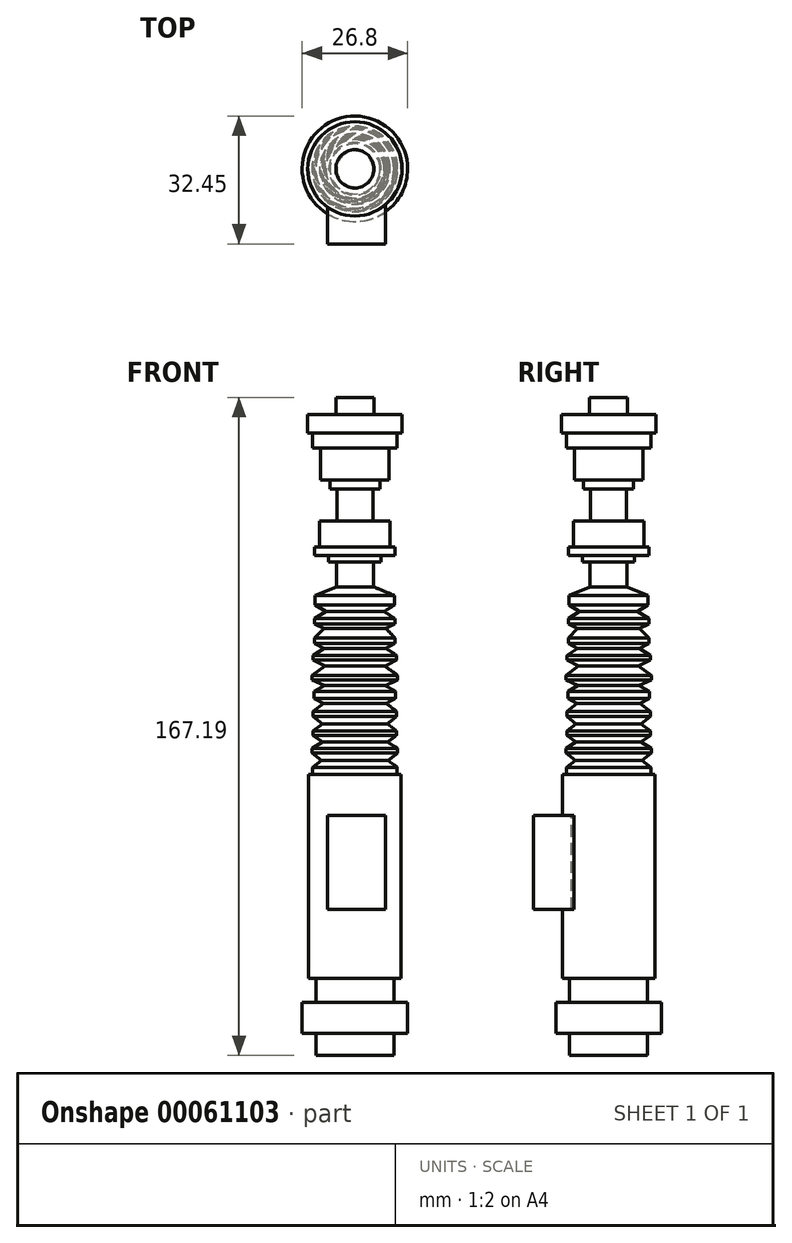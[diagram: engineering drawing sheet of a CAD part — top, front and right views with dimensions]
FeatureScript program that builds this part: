
annotation { "Feature Type Name" : "Feature", "Feature Type Description" : "" }
export const myFeature = defineFeature(function(context is Context, id is Id, definition is map)
    precondition{}
    {
        {
            var Q0;
            Q0=qCreatedBy(makeId("Front.planeOp"),FACE);
            var sketch = newSketch(context, id + "F0", { "sketchPlane" : qUnion([Q0])});
            skLineSegment(sketch, "E0", {"start": v(0, 232.03) * mm, "end": v(0, 0) * mm});
            skLineSegment(sketch, "E1", {"start": v(0, 178.73) * mm, "end": v(4.85, 178.73) * mm});
            skLineSegment(sketch, "E2", {"start": v(4.85, 178.73) * mm, "end": v(4.85, 174.35) * mm});
            skLineSegment(sketch, "E3", {"start": v(4.85, 174.35) * mm, "end": v(11.98, 174.35) * mm});
            skLineSegment(sketch, "E4", {"start": v(11.98, 174.35) * mm, "end": v(11.98, 169.68) * mm});
            skLineSegment(sketch, "E5", {"start": v(11.98, 169.68) * mm, "end": v(10.75, 169.68) * mm});
            skLineSegment(sketch, "E6", {"start": v(10.75, 169.68) * mm, "end": v(10.75, 165.85) * mm});
            skLineSegment(sketch, "E7", {"start": v(10.75, 165.85) * mm, "end": v(8.7, 165.85) * mm});
            skLineSegment(sketch, "E8", {"start": v(8.7, 165.85) * mm, "end": v(8.7, 157.76) * mm});
            skLineSegment(sketch, "E9", {"start": v(8.7, 157.76) * mm, "end": v(6.36, 157.76) * mm});
            skLineSegment(sketch, "E10", {"start": v(6.36, 157.76) * mm, "end": v(6.36, 155.43) * mm});
            skLineSegment(sketch, "E11", {"start": v(6.36, 155.43) * mm, "end": v(4.58, 155.43) * mm});
            skLineSegment(sketch, "E12", {"start": v(4.58, 155.43) * mm, "end": v(4.58, 147.34) * mm});
            skLineSegment(sketch, "E13", {"start": v(4.58, 147.34) * mm, "end": v(8.97, 147.34) * mm});
            skLineSegment(sketch, "E14", {"start": v(8.97, 147.34) * mm, "end": v(8.97, 140.75) * mm});
            skLineSegment(sketch, "E15", {"start": v(8.97, 140.75) * mm, "end": v(10.2, 140.75) * mm});
            skLineSegment(sketch, "E16", {"start": v(10.2, 140.75) * mm, "end": v(10.2, 138.56) * mm});
            skLineSegment(sketch, "E17", {"start": v(10.2, 138.56) * mm, "end": v(6.64, 138.56) * mm});
            skLineSegment(sketch, "E18", {"start": v(6.64, 138.56) * mm, "end": v(6.64, 136.92) * mm});
            skLineSegment(sketch, "E19", {"start": v(6.64, 136.92) * mm, "end": v(4.72, 136.92) * mm});
            skLineSegment(sketch, "E20", {"start": v(4.72, 136.92) * mm, "end": v(4.72, 130.6) * mm});
            skLineSegment(sketch, "E21", {"start": v(4.72, 130.6) * mm, "end": v(10.06, 128.38) * mm});
            skLineSegment(sketch, "E22", {"start": v(10.06, 128.38) * mm, "end": v(10.06, 125.95) * mm});
            skLineSegment(sketch, "E23", {"start": v(10.06, 125.95) * mm, "end": v(7.39, 124.3) * mm});
            skPoint(sketch, "E23.endSnap0", {"position": v(7.39, 129.5) * mm});
            skLineSegment(sketch, "E24", {"start": v(7.39, 124.3) * mm, "end": v(10.2, 122.52) * mm});
            skLineSegment(sketch, "E25", {"start": v(10.2, 122.52) * mm, "end": v(10.2, 121.15) * mm});
            skLineSegment(sketch, "E26", {"start": v(10.2, 121.15) * mm, "end": v(7.87, 120.05) * mm});
            skLineSegment(sketch, "E27", {"start": v(7.87, 120.05) * mm, "end": v(10.2, 117.58) * mm});
            skLineSegment(sketch, "E28", {"start": v(10.2, 117.58) * mm, "end": v(10.2, 116.21) * mm});
            skLineSegment(sketch, "E29", {"start": v(10.2, 116.21) * mm, "end": v(7.87, 114.98) * mm});
            skLineSegment(sketch, "E30", {"start": v(7.87, 114.98) * mm, "end": v(10.61, 113.2) * mm});
            skLineSegment(sketch, "E31", {"start": v(10.61, 113.2) * mm, "end": v(10.61, 111.96) * mm});
            skLineSegment(sketch, "E32", {"start": v(10.61, 111.96) * mm, "end": v(7.6, 110.45) * mm});
            skLineSegment(sketch, "E33", {"start": v(7.6, 110.45) * mm, "end": v(10.89, 108.12) * mm});
            skLineSegment(sketch, "E34", {"start": v(10.89, 108.12) * mm, "end": v(10.89, 106.89) * mm});
            skLineSegment(sketch, "E35", {"start": v(10.89, 106.89) * mm, "end": v(7.73, 105.52) * mm});
            skLineSegment(sketch, "E36", {"start": v(7.73, 105.52) * mm, "end": v(10.34, 104) * mm});
            skLineSegment(sketch, "E37", {"start": v(10.34, 104) * mm, "end": v(10.34, 102.23) * mm});
            skLineSegment(sketch, "E38", {"start": v(10.34, 102.23) * mm, "end": v(8, 101) * mm});
            skLineSegment(sketch, "E39", {"start": v(8, 101) * mm, "end": v(10.61, 98.94) * mm});
            skLineSegment(sketch, "E40", {"start": v(10.61, 98.94) * mm, "end": v(10.61, 97.7) * mm});
            skLineSegment(sketch, "E41", {"start": v(10.61, 97.7) * mm, "end": v(8.28, 95.78) * mm});
            skLineSegment(sketch, "E42", {"start": v(8.28, 95.78) * mm, "end": v(10.61, 93.94) * mm});
            skLineSegment(sketch, "E43", {"start": v(10.61, 93.94) * mm, "end": v(10.61, 92.89) * mm});
            skLineSegment(sketch, "E44", {"start": v(10.61, 92.89) * mm, "end": v(8.28, 91.14) * mm});
            skLineSegment(sketch, "E45", {"start": v(8.28, 91.14) * mm, "end": v(10.85, 89.59) * mm});
            skLineSegment(sketch, "E46", {"start": v(10.85, 89.59) * mm, "end": v(10.85, 88.33) * mm});
            skLineSegment(sketch, "E47", {"start": v(10.85, 88.33) * mm, "end": v(8.42, 86.49) * mm});
            skLineSegment(sketch, "E48", {"start": v(8.42, 86.49) * mm, "end": v(10.75, 84.74) * mm});
            skLineSegment(sketch, "E49", {"start": v(10.75, 84.74) * mm, "end": v(10.75, 82.9) * mm});
            skLineSegment(sketch, "E50", {"start": v(10.75, 82.9) * mm, "end": v(11.72, 82.9) * mm});
            skLineSegment(sketch, "E51", {"start": v(11.72, 82.9) * mm, "end": v(11.72, 31.09) * mm});
            skLineSegment(sketch, "E52", {"start": v(11.72, 31.09) * mm, "end": v(9.92, 31.09) * mm});
            skLineSegment(sketch, "E53", {"start": v(9.92, 31.09) * mm, "end": v(9.92, 25.03) * mm});
            skLineSegment(sketch, "E54", {"start": v(9.92, 25.03) * mm, "end": v(13.4, 25.03) * mm});
            skLineSegment(sketch, "E55", {"start": v(13.4, 25.03) * mm, "end": v(13.4, 17.2) * mm});
            skLineSegment(sketch, "E56", {"start": v(9.92, 17.2) * mm, "end": v(9.92, 11.54) * mm});
            skLineSegment(sketch, "E57", {"start": v(9.92, 11.54) * mm, "end": v(0, 11.54) * mm});
            skLineSegment(sketch, "E58", {"start": v(0, 11.54) * mm, "end": v(0, 178.73) * mm});
            skLineSegment(sketch, "E59", {"start": v(0, 178.73) * mm, "end": v(0, 11.54) * mm});
            skLineSegment(sketch, "E60", {"start": v(9.92, 17.2) * mm, "end": v(13.4, 17.2) * mm});
            skSolve(sketch);
        }
        {
            var Q0;
            Q0=makeQuery(id+"F0.imprint","IMPRINT",FACE,{"disambiguationData":[TD([[makeQuery(id+"F0.imprint","IMPRINT",EDGE,{"derivedFrom":sQuery(id+"F0.wireOp",EDGE,"E1")}),-1.0]])]});
            var Q1;
            Q1=sQuery(id+"F0.wireOp",EDGE,"E0");
            revolve(context, id + "F1", {"entities" : qUnion([Q0]), "axis" : qUnion([Q1]), "revolveType" : RevolveType.FULL});
        }
        {
            var Q0;
            Q0=qCreatedBy(makeId("Front.planeOp"),FACE);
            cPlane(context, id + "F2", {"entities" : qUnion([Q0]), "cplaneType" : CPlaneType.OFFSET, "offset" : 19.05 * mm, "width" : 152.4 * mm, "height" : 152.4 * mm});
        }
        {
            var Q0;
            Q0=qCreatedBy(id+"F2.planeOp",FACE);
            var sketch = newSketch(context, id + "F3", { "sketchPlane" : qUnion([Q0])});
            skLineSegment(sketch, "E61.bottom", {"start": v(-6.98, 72.52) * mm, "end": v(7.8, 72.52) * mm});
            skLineSegment(sketch, "E61.top", {"start": v(-6.98, 48.69) * mm, "end": v(7.8, 48.69) * mm});
            skLineSegment(sketch, "E61.left", {"start": v(-6.98, 72.52) * mm, "end": v(-6.98, 48.69) * mm});
            skLineSegment(sketch, "E61.right", {"start": v(7.8, 72.52) * mm, "end": v(7.8, 48.69) * mm});
            skSolve(sketch);
        }
        {
            var Q0;
            Q0=makeQuery(id+"F3.imprint","IMPRINT",FACE,{"disambiguationData":[TD([[makeQuery(id+"F3.imprint","IMPRINT",EDGE,{"derivedFrom":sQuery(id+"F3.wireOp",EDGE,"E61.bottom")}),-1.0]])]});
            extrude(context, id + "F4", {"entities" : qUnion([Q0]), "operationType" : NewBodyOperationType.ADD, "endBound" : BoundingType.UP_TO_NEXT, "oppositeDirection" : true, "depth" : 25.4 * mm});
        }
    });
